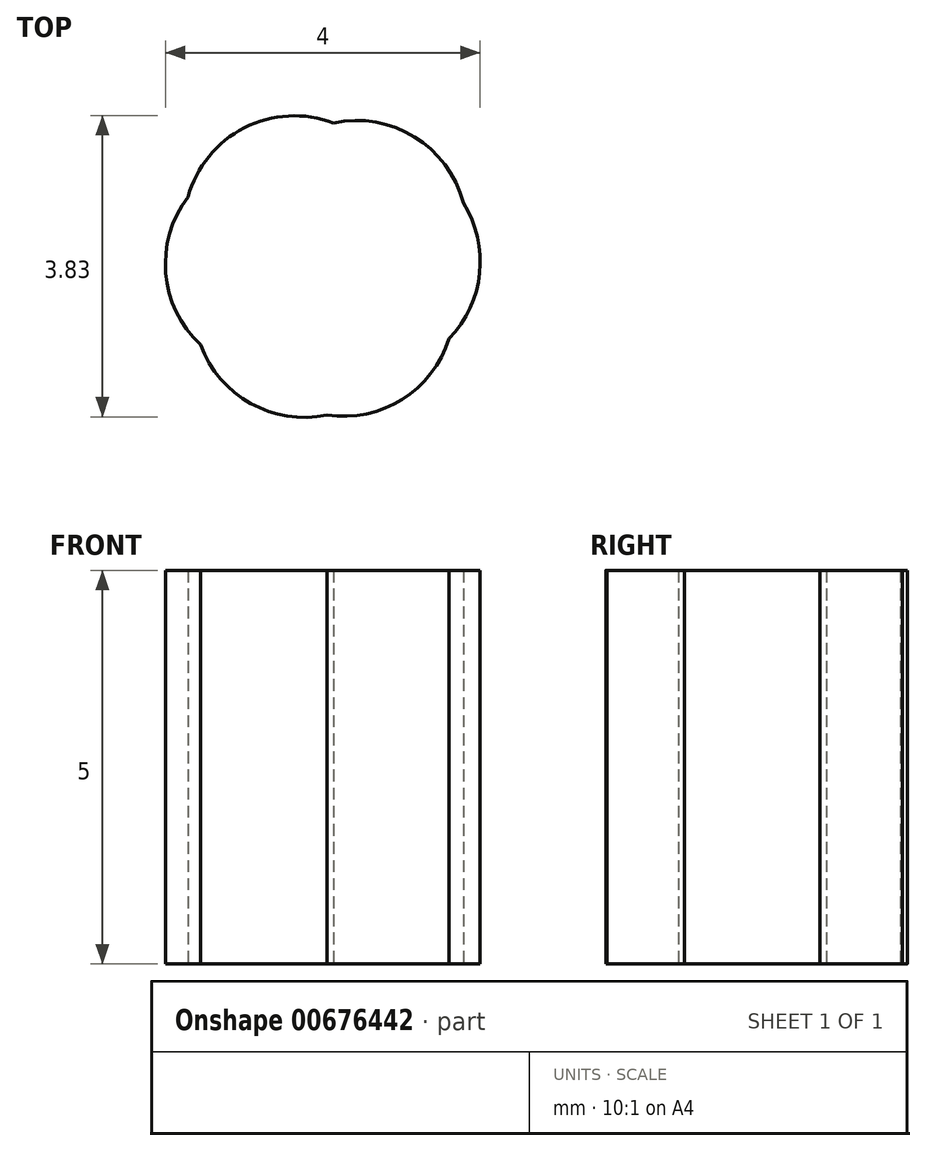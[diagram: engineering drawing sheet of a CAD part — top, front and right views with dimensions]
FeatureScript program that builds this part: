
annotation { "Feature Type Name" : "Feature", "Feature Type Description" : "" }
export const myFeature = defineFeature(function(context is Context, id is Id, definition is map)
    precondition{}
    {
        {
            var Q0;
            Q0=qCreatedBy(makeId("Top.planeOp"),FACE);
            var sketch = newSketch(context, id + "F0", { "sketchPlane" : qUnion([Q0])});
            skCircle(sketch, "E0", {"center": v(-2.25, 0.1) * mm, "radius": 1.4 * mm});
            skCircle(sketch, "E1", {"center": v(-1.88, -0.45) * mm, "radius": 1.4 * mm});
            skCircle(sketch, "E2", {"center": v(-1.05, 0.12) * mm, "radius": 1.4 * mm});
            skCircle(sketch, "E3", {"center": v(-1.22, 0.52) * mm, "radius": 1.4 * mm});
            skCircle(sketch, "E4", {"center": v(-2.01, 0.58) * mm, "radius": 1.4 * mm});
            skCircle(sketch, "E5", {"center": v(-1.38, -0.44) * mm, "radius": 1.4 * mm});
            skSolve(sketch);
        }
        {
            var Q0;
            {var subQ0=sQuery(id+"F0.wireOp",EDGE,"E3");var subQ1=sQuery(id+"F0.wireOp",EDGE,"E2");var subQ2=makeQuery(id+"F0.imprint","INTERSECT",VERTEX,{"disambiguationData":[OD(0.0)],"derivedFrom":[subQ1,subQ0]});Q0=makeQuery(id+"F0.imprint","IMPRINT",FACE,{"disambiguationData":[TD([[makeQuery(id+"F0.imprint","IMPRINT",EDGE,{"disambiguationData":[TD([[subQ2,1.0]])],"derivedFrom":subQ1}),1.0]])]});}
            var Q1;
            {var subQ0=sQuery(id+"F0.wireOp",EDGE,"E5");var subQ1=sQuery(id+"F0.wireOp",EDGE,"E0");var subQ2=makeQuery(id+"F0.imprint","INTERSECT",VERTEX,{"disambiguationData":[OD(0.0)],"derivedFrom":[subQ1,subQ0]});Q1=makeQuery(id+"F0.imprint","IMPRINT",FACE,{"disambiguationData":[TD([[makeQuery(id+"F0.imprint","IMPRINT",EDGE,{"disambiguationData":[TD([[subQ2,-1.0]])],"derivedFrom":subQ1}),-1.0]])]});}
            var Q2;
            {var subQ0=sQuery(id+"F0.wireOp",EDGE,"E1");var subQ1=sQuery(id+"F0.wireOp",EDGE,"E0");var subQ2=makeQuery(id+"F0.imprint","INTERSECT",VERTEX,{"disambiguationData":[OD(0.0)],"derivedFrom":[subQ1,subQ0]});Q2=makeQuery(id+"F0.imprint","IMPRINT",FACE,{"disambiguationData":[TD([[makeQuery(id+"F0.imprint","IMPRINT",EDGE,{"disambiguationData":[TD([[subQ2,-1.0]])],"derivedFrom":subQ1}),-1.0]])]});}
            var Q3;
            {var subQ0=sQuery(id+"F0.wireOp",EDGE,"E2");var subQ1=sQuery(id+"F0.wireOp",EDGE,"E1");var subQ2=makeQuery(id+"F0.imprint","INTERSECT",VERTEX,{"disambiguationData":[OD(1.0)],"derivedFrom":[subQ1,subQ0]});Q3=makeQuery(id+"F0.imprint","IMPRINT",FACE,{"disambiguationData":[TD([[makeQuery(id+"F0.imprint","IMPRINT",EDGE,{"disambiguationData":[TD([[subQ2,-1.0]])],"derivedFrom":subQ1}),-1.0]])]});}
            var Q4;
            {var subQ0=sQuery(id+"F0.wireOp",EDGE,"E4");var subQ1=sQuery(id+"F0.wireOp",EDGE,"E0");var subQ2=makeQuery(id+"F0.imprint","INTERSECT",VERTEX,{"disambiguationData":[OD(0.0)],"derivedFrom":[subQ1,subQ0]});Q4=makeQuery(id+"F0.imprint","IMPRINT",FACE,{"disambiguationData":[TD([[makeQuery(id+"F0.imprint","IMPRINT",EDGE,{"disambiguationData":[TD([[subQ2,1.0]])],"derivedFrom":subQ1}),1.0]])]});}
            var Q5;
            {var subQ0=sQuery(id+"F0.wireOp",EDGE,"E4");var subQ1=sQuery(id+"F0.wireOp",EDGE,"E0");var subQ2=makeQuery(id+"F0.imprint","INTERSECT",VERTEX,{"disambiguationData":[OD(0.0)],"derivedFrom":[subQ1,subQ0]});Q5=makeQuery(id+"F0.imprint","IMPRINT",FACE,{"disambiguationData":[TD([[makeQuery(id+"F0.imprint","IMPRINT",EDGE,{"disambiguationData":[TD([[subQ2,-1.0]])],"derivedFrom":subQ1}),1.0]])]});}
            var Q6;
            {var subQ0=sQuery(id+"F0.wireOp",EDGE,"E5");var subQ1=sQuery(id+"F0.wireOp",EDGE,"E0");var subQ2=makeQuery(id+"F0.imprint","INTERSECT",VERTEX,{"disambiguationData":[OD(0.0)],"derivedFrom":[subQ1,subQ0]});Q6=makeQuery(id+"F0.imprint","IMPRINT",FACE,{"disambiguationData":[TD([[makeQuery(id+"F0.imprint","IMPRINT",EDGE,{"disambiguationData":[TD([[subQ2,1.0]])],"derivedFrom":subQ1}),1.0]])]});}
            var Q7;
            {var subQ0=sQuery(id+"F0.wireOp",EDGE,"E3");var subQ1=sQuery(id+"F0.wireOp",EDGE,"E2");var subQ2=makeQuery(id+"F0.imprint","INTERSECT",VERTEX,{"disambiguationData":[OD(0.0)],"derivedFrom":[subQ1,subQ0]});Q7=makeQuery(id+"F0.imprint","IMPRINT",FACE,{"disambiguationData":[TD([[makeQuery(id+"F0.imprint","IMPRINT",EDGE,{"disambiguationData":[TD([[subQ2,-1.0]])],"derivedFrom":subQ1}),-1.0]])]});}
            var Q8;
            {var subQ0=sQuery(id+"F0.wireOp",EDGE,"E3");var subQ1=sQuery(id+"F0.wireOp",EDGE,"E0");var subQ2=makeQuery(id+"F0.imprint","INTERSECT",VERTEX,{"disambiguationData":[OD(1.0)],"derivedFrom":[subQ1,subQ0]});Q8=makeQuery(id+"F0.imprint","IMPRINT",FACE,{"disambiguationData":[TD([[makeQuery(id+"F0.imprint","IMPRINT",EDGE,{"disambiguationData":[TD([[subQ2,-1.0]])],"derivedFrom":subQ1}),1.0]])]});}
            var Q9;
            {var subQ0=sQuery(id+"F0.wireOp",EDGE,"E4");var subQ1=sQuery(id+"F0.wireOp",EDGE,"E0");var subQ2=makeQuery(id+"F0.imprint","INTERSECT",VERTEX,{"disambiguationData":[OD(0.0)],"derivedFrom":[subQ1,subQ0]});Q9=makeQuery(id+"F0.imprint","IMPRINT",FACE,{"disambiguationData":[TD([[makeQuery(id+"F0.imprint","IMPRINT",EDGE,{"disambiguationData":[TD([[subQ2,1.0]])],"derivedFrom":subQ1}),-1.0]])]});}
            var Q10;
            {var subQ0=sQuery(id+"F0.wireOp",EDGE,"E3");var subQ1=sQuery(id+"F0.wireOp",EDGE,"E2");var subQ2=makeQuery(id+"F0.imprint","INTERSECT",VERTEX,{"disambiguationData":[OD(1.0)],"derivedFrom":[subQ1,subQ0]});Q10=makeQuery(id+"F0.imprint","IMPRINT",FACE,{"disambiguationData":[TD([[makeQuery(id+"F0.imprint","IMPRINT",EDGE,{"disambiguationData":[TD([[subQ2,-1.0]])],"derivedFrom":subQ1}),-1.0]])]});}
            var Q11;
            {var subQ0=sQuery(id+"F0.wireOp",EDGE,"E3");var subQ1=sQuery(id+"F0.wireOp",EDGE,"E2");var subQ2=makeQuery(id+"F0.imprint","INTERSECT",VERTEX,{"disambiguationData":[OD(0.0)],"derivedFrom":[subQ1,subQ0]});Q11=makeQuery(id+"F0.imprint","IMPRINT",FACE,{"disambiguationData":[TD([[makeQuery(id+"F0.imprint","IMPRINT",EDGE,{"disambiguationData":[TD([[subQ2,-1.0]])],"derivedFrom":subQ1}),1.0]])]});}
            var Q12;
            {var subQ0=sQuery(id+"F0.wireOp",EDGE,"E2");var subQ1=sQuery(id+"F0.wireOp",EDGE,"E1");var subQ2=makeQuery(id+"F0.imprint","INTERSECT",VERTEX,{"disambiguationData":[OD(0.0)],"derivedFrom":[subQ1,subQ0]});Q12=makeQuery(id+"F0.imprint","IMPRINT",FACE,{"disambiguationData":[TD([[makeQuery(id+"F0.imprint","IMPRINT",EDGE,{"disambiguationData":[TD([[subQ2,-1.0]])],"derivedFrom":subQ1}),1.0]])]});}
            var Q13;
            {var subQ0=sQuery(id+"F0.wireOp",EDGE,"E5");var subQ1=sQuery(id+"F0.wireOp",EDGE,"E0");var subQ2=makeQuery(id+"F0.imprint","INTERSECT",VERTEX,{"disambiguationData":[OD(1.0)],"derivedFrom":[subQ1,subQ0]});Q13=makeQuery(id+"F0.imprint","IMPRINT",FACE,{"disambiguationData":[TD([[makeQuery(id+"F0.imprint","IMPRINT",EDGE,{"disambiguationData":[TD([[subQ2,-1.0]])],"derivedFrom":subQ1}),-1.0]])]});}
            var Q14;
            {var subQ0=sQuery(id+"F0.wireOp",EDGE,"E2");var subQ1=sQuery(id+"F0.wireOp",EDGE,"E0");var subQ2=makeQuery(id+"F0.imprint","INTERSECT",VERTEX,{"disambiguationData":[OD(0.0)],"derivedFrom":[subQ1,subQ0]});Q14=makeQuery(id+"F0.imprint","IMPRINT",FACE,{"disambiguationData":[TD([[makeQuery(id+"F0.imprint","IMPRINT",EDGE,{"disambiguationData":[TD([[subQ2,-1.0]])],"derivedFrom":subQ1}),-1.0]])]});}
            var Q15;
            {var subQ0=sQuery(id+"F0.wireOp",EDGE,"E3");var subQ1=sQuery(id+"F0.wireOp",EDGE,"E2");var subQ2=makeQuery(id+"F0.imprint","INTERSECT",VERTEX,{"disambiguationData":[OD(1.0)],"derivedFrom":[subQ1,subQ0]});Q15=makeQuery(id+"F0.imprint","IMPRINT",FACE,{"disambiguationData":[TD([[makeQuery(id+"F0.imprint","IMPRINT",EDGE,{"disambiguationData":[TD([[subQ2,-1.0]])],"derivedFrom":subQ1}),1.0]])]});}
            var Q16;
            {var subQ0=sQuery(id+"F0.wireOp",EDGE,"E5");var subQ1=sQuery(id+"F0.wireOp",EDGE,"E0");var subQ2=makeQuery(id+"F0.imprint","INTERSECT",VERTEX,{"disambiguationData":[OD(0.0)],"derivedFrom":[subQ1,subQ0]});Q16=makeQuery(id+"F0.imprint","IMPRINT",FACE,{"disambiguationData":[TD([[makeQuery(id+"F0.imprint","IMPRINT",EDGE,{"disambiguationData":[TD([[subQ2,-1.0]])],"derivedFrom":subQ1}),1.0]])]});}
            var Q17;
            {var subQ7=sQuery(id+"F0.wireOp",EDGE,"E1");var subQ8=sQuery(id+"F0.wireOp",EDGE,"E0");var subQ9=makeQuery(id+"F0.imprint","INTERSECT",VERTEX,{"disambiguationData":[OD(1.0)],"derivedFrom":[subQ8,subQ7]});Q17=makeQuery(id+"F0.imprint","IMPRINT",FACE,{"disambiguationData":[TD([[makeQuery(id+"F0.imprint","IMPRINT",EDGE,{"disambiguationData":[TD([[subQ9,1.0]])],"derivedFrom":subQ8}),1.0]])]});}
            var Q18;
            {var subQ0=sQuery(id+"F0.wireOp",EDGE,"E5");var subQ1=sQuery(id+"F0.wireOp",EDGE,"E1");var subQ2=makeQuery(id+"F0.imprint","INTERSECT",VERTEX,{"disambiguationData":[OD(1.0)],"derivedFrom":[subQ1,subQ0]});Q18=makeQuery(id+"F0.imprint","IMPRINT",FACE,{"disambiguationData":[TD([[makeQuery(id+"F0.imprint","IMPRINT",EDGE,{"disambiguationData":[TD([[subQ2,-1.0]])],"derivedFrom":subQ1}),1.0]])]});}
            var Q19;
            {var subQ0=sQuery(id+"F0.wireOp",EDGE,"E3");var subQ1=sQuery(id+"F0.wireOp",EDGE,"E0");var subQ2=makeQuery(id+"F0.imprint","INTERSECT",VERTEX,{"disambiguationData":[OD(1.0)],"derivedFrom":[subQ1,subQ0]});Q19=makeQuery(id+"F0.imprint","IMPRINT",FACE,{"disambiguationData":[TD([[makeQuery(id+"F0.imprint","IMPRINT",EDGE,{"disambiguationData":[TD([[subQ2,-1.0]])],"derivedFrom":subQ1}),-1.0]])]});}
            var Q20;
            {var subQ0=sQuery(id+"F0.wireOp",EDGE,"E4");var subQ1=sQuery(id+"F0.wireOp",EDGE,"E1");var subQ2=makeQuery(id+"F0.imprint","INTERSECT",VERTEX,{"disambiguationData":[OD(0.0)],"derivedFrom":[subQ1,subQ0]});Q20=makeQuery(id+"F0.imprint","IMPRINT",FACE,{"disambiguationData":[TD([[makeQuery(id+"F0.imprint","IMPRINT",EDGE,{"disambiguationData":[TD([[subQ2,1.0]])],"derivedFrom":subQ1}),-1.0]])]});}
            var Q21;
            {var subQ0=sQuery(id+"F0.wireOp",EDGE,"E1");var subQ1=sQuery(id+"F0.wireOp",EDGE,"E0");var subQ2=makeQuery(id+"F0.imprint","INTERSECT",VERTEX,{"disambiguationData":[OD(1.0)],"derivedFrom":[subQ1,subQ0]});Q21=makeQuery(id+"F0.imprint","IMPRINT",FACE,{"disambiguationData":[TD([[makeQuery(id+"F0.imprint","IMPRINT",EDGE,{"disambiguationData":[TD([[subQ2,1.0]])],"derivedFrom":subQ1}),-1.0]])]});}
            var Q22;
            {var subQ0=sQuery(id+"F0.wireOp",EDGE,"E5");var subQ1=sQuery(id+"F0.wireOp",EDGE,"E0");var subQ2=makeQuery(id+"F0.imprint","INTERSECT",VERTEX,{"disambiguationData":[OD(0.0)],"derivedFrom":[subQ1,subQ0]});Q22=makeQuery(id+"F0.imprint","IMPRINT",FACE,{"disambiguationData":[TD([[makeQuery(id+"F0.imprint","IMPRINT",EDGE,{"disambiguationData":[TD([[subQ2,1.0]])],"derivedFrom":subQ1}),-1.0]])]});}
            var Q23;
            {var subQ0=sQuery(id+"F0.wireOp",EDGE,"E5");var subQ1=sQuery(id+"F0.wireOp",EDGE,"E2");var subQ2=makeQuery(id+"F0.imprint","INTERSECT",VERTEX,{"disambiguationData":[OD(1.0)],"derivedFrom":[subQ1,subQ0]});Q23=makeQuery(id+"F0.imprint","IMPRINT",FACE,{"disambiguationData":[TD([[makeQuery(id+"F0.imprint","IMPRINT",EDGE,{"disambiguationData":[TD([[subQ2,-1.0]])],"derivedFrom":subQ1}),-1.0]])]});}
            var Q24;
            {var subQ0=sQuery(id+"F0.wireOp",EDGE,"E5");var subQ1=sQuery(id+"F0.wireOp",EDGE,"E1");var subQ2=makeQuery(id+"F0.imprint","INTERSECT",VERTEX,{"disambiguationData":[OD(0.0)],"derivedFrom":[subQ1,subQ0]});Q24=makeQuery(id+"F0.imprint","IMPRINT",FACE,{"disambiguationData":[TD([[makeQuery(id+"F0.imprint","IMPRINT",EDGE,{"disambiguationData":[TD([[subQ2,-1.0]])],"derivedFrom":subQ1}),-1.0]])]});}
            var Q25;
            {var subQ0=sQuery(id+"F0.wireOp",EDGE,"E3");var subQ1=sQuery(id+"F0.wireOp",EDGE,"E1");var subQ2=makeQuery(id+"F0.imprint","INTERSECT",VERTEX,{"disambiguationData":[OD(0.0)],"derivedFrom":[subQ1,subQ0]});Q25=makeQuery(id+"F0.imprint","IMPRINT",FACE,{"disambiguationData":[TD([[makeQuery(id+"F0.imprint","IMPRINT",EDGE,{"disambiguationData":[TD([[subQ2,-1.0]])],"derivedFrom":subQ1}),1.0]])]});}
            var Q26;
            {var subQ0=sQuery(id+"F0.wireOp",EDGE,"E1");var subQ1=sQuery(id+"F0.wireOp",EDGE,"E0");var subQ2=makeQuery(id+"F0.imprint","INTERSECT",VERTEX,{"disambiguationData":[OD(0.0)],"derivedFrom":[subQ1,subQ0]});Q26=makeQuery(id+"F0.imprint","IMPRINT",FACE,{"disambiguationData":[TD([[makeQuery(id+"F0.imprint","IMPRINT",EDGE,{"disambiguationData":[TD([[subQ2,-1.0]])],"derivedFrom":subQ1}),1.0]])]});}
            var Q27;
            {var subQ0=sQuery(id+"F0.wireOp",EDGE,"E2");var subQ1=sQuery(id+"F0.wireOp",EDGE,"E0");var subQ2=makeQuery(id+"F0.imprint","INTERSECT",VERTEX,{"disambiguationData":[OD(0.0)],"derivedFrom":[subQ1,subQ0]});Q27=makeQuery(id+"F0.imprint","IMPRINT",FACE,{"disambiguationData":[TD([[makeQuery(id+"F0.imprint","IMPRINT",EDGE,{"disambiguationData":[TD([[subQ2,-1.0]])],"derivedFrom":subQ1}),1.0]])]});}
            var Q28;
            {var subQ0=sQuery(id+"F0.wireOp",EDGE,"E5");var subQ1=sQuery(id+"F0.wireOp",EDGE,"E0");var subQ2=makeQuery(id+"F0.imprint","INTERSECT",VERTEX,{"disambiguationData":[OD(1.0)],"derivedFrom":[subQ1,subQ0]});Q28=makeQuery(id+"F0.imprint","IMPRINT",FACE,{"disambiguationData":[TD([[makeQuery(id+"F0.imprint","IMPRINT",EDGE,{"disambiguationData":[TD([[subQ2,-1.0]])],"derivedFrom":subQ1}),1.0]])]});}
            var Q29;
            {var subQ0=sQuery(id+"F0.wireOp",EDGE,"E2");var subQ1=sQuery(id+"F0.wireOp",EDGE,"E0");var subQ2=makeQuery(id+"F0.imprint","INTERSECT",VERTEX,{"disambiguationData":[OD(1.0)],"derivedFrom":[subQ1,subQ0]});Q29=makeQuery(id+"F0.imprint","IMPRINT",FACE,{"disambiguationData":[TD([[makeQuery(id+"F0.imprint","IMPRINT",EDGE,{"disambiguationData":[TD([[subQ2,-1.0]])],"derivedFrom":subQ1}),-1.0]])]});}
            var Q30;
            {var subQ0=sQuery(id+"F0.wireOp",EDGE,"E2");var subQ1=sQuery(id+"F0.wireOp",EDGE,"E0");var subQ2=makeQuery(id+"F0.imprint","INTERSECT",VERTEX,{"disambiguationData":[OD(1.0)],"derivedFrom":[subQ1,subQ0]});Q30=makeQuery(id+"F0.imprint","IMPRINT",FACE,{"disambiguationData":[TD([[makeQuery(id+"F0.imprint","IMPRINT",EDGE,{"disambiguationData":[TD([[subQ2,-1.0]])],"derivedFrom":subQ1}),1.0]])]});}
            extrude(context, id + "F1", {"entities" : qUnion([Q0, Q1, Q2, Q3, Q4, Q5, Q6, Q7, Q8, Q9, Q10, Q11, Q12, Q13, Q14, Q15, Q16, Q17, Q18, Q19, Q20, Q21, Q22, Q23, Q24, Q25, Q26, Q27, Q28, Q29, Q30]), "depth" : 5 * mm, "offsetDistance" : 25 * mm});
        }
    });
